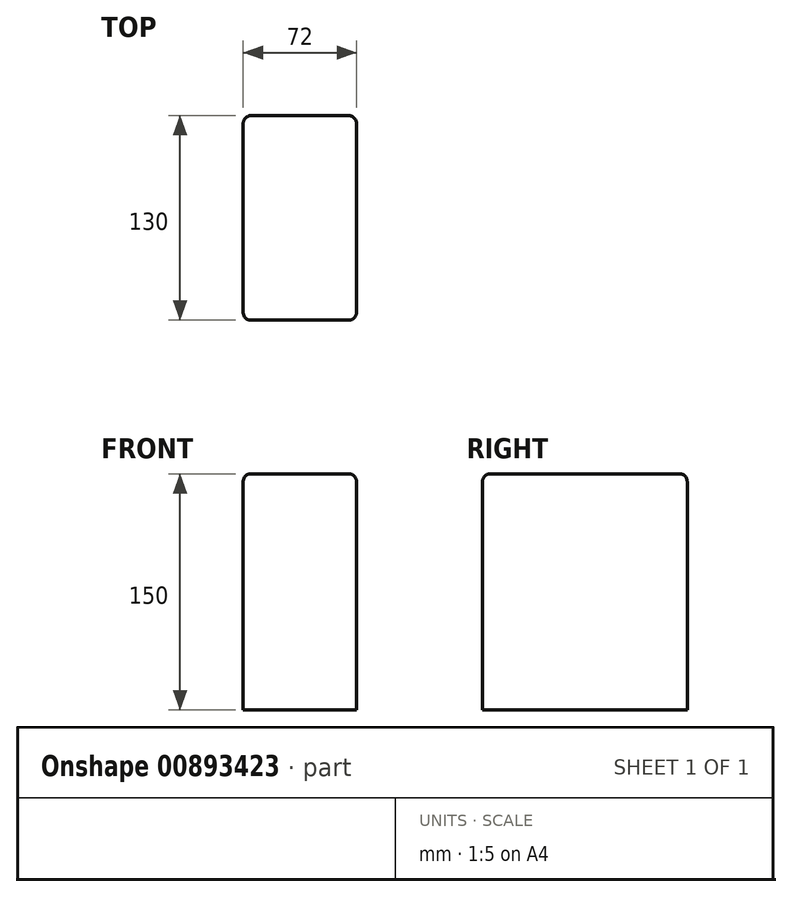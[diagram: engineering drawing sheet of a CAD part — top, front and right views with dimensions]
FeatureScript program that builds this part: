
annotation { "Feature Type Name" : "Feature", "Feature Type Description" : "" }
export const myFeature = defineFeature(function(context is Context, id is Id, definition is map)
    precondition{}
    {
        {
            var Q0;
            Q0=qCreatedBy(makeId("Top.planeOp"), FACE);
            var sketch = newSketch(context, id + "F0", { "sketchPlane" : qUnion([Q0])});
            skLineSegment(sketch, "E0.bottom", {"start": v(-72, 130) * mm, "end": v(0, 130) * mm});
            skLineSegment(sketch, "E0.top", {"start": v(-72, 0) * mm, "end": v(0, 0) * mm});
            skLineSegment(sketch, "E0.left", {"start": v(-72, 130) * mm, "end": v(-72, 0) * mm});
            skLineSegment(sketch, "E0.right", {"start": v(0, 130) * mm, "end": v(0, 0) * mm});
            skSolve(sketch);
        }
        {
            var Q0;
            Q0=makeQuery(id+"F0.imprint","IMPRINT",FACE,{"disambiguationData":[TD([[makeQuery(id+"F0.imprint","IMPRINT",EDGE,{"derivedFrom":sQuery(id+"F0.wireOp",EDGE,"E0.bottom")}),-1.0]])]});
            extrude(context, id + "F1", {"entities" : qUnion([Q0]), "depth" : 150 * mm, "offsetDistance" : 25 * mm});
        }
        {
            var Q0;
            Q0=makeQuery(id+"F1.opExtrude","CAP_FACE",FACE,{"disambiguationData":[OSD([sQuery(id+"F0.wireOp",EDGE,"E0.bottom"),sQuery(id+"F0.wireOp",EDGE,"E0.top"),sQuery(id+"F0.wireOp",EDGE,"E0.left"),sQuery(id+"F0.wireOp",EDGE,"E0.right")])],"isStart":false});
            var Q1;
            Q1=makeQuery(id+"F1.opExtrude","SWEPT_EDGE",EDGE,{"disambiguationData":[OSD([sQuery(id+"F0.wireOp",EDGE,"E0.top"),sQuery(id+"F0.wireOp",EDGE,"E0.right")])]});
            var Q2;
            Q2=makeQuery(id+"F1.opExtrude","SWEPT_EDGE",EDGE,{"disambiguationData":[OSD([sQuery(id+"F0.wireOp",EDGE,"E0.top"),sQuery(id+"F0.wireOp",EDGE,"E0.left")])]});
            var Q3;
            Q3=makeQuery(id+"F1.opExtrude","SWEPT_EDGE",EDGE,{"disambiguationData":[OSD([sQuery(id+"F0.wireOp",EDGE,"E0.bottom"),sQuery(id+"F0.wireOp",EDGE,"E0.right")])]});
            var Q4;
            Q4=makeQuery(id+"F1.opExtrude","SWEPT_EDGE",EDGE,{"disambiguationData":[OSD([sQuery(id+"F0.wireOp",EDGE,"E0.bottom"),sQuery(id+"F0.wireOp",EDGE,"E0.left")])]});
            fillet(context, id + "F2", {"entities" : qUnion([Q0, Q1, Q2, Q3, Q4]), "tangentPropagation" : true, "radius" : 5 * mm, "defaultsChanged" : false, "vertexSettings" : [], "allowEdgeOverflow" : false});
        }
    });
